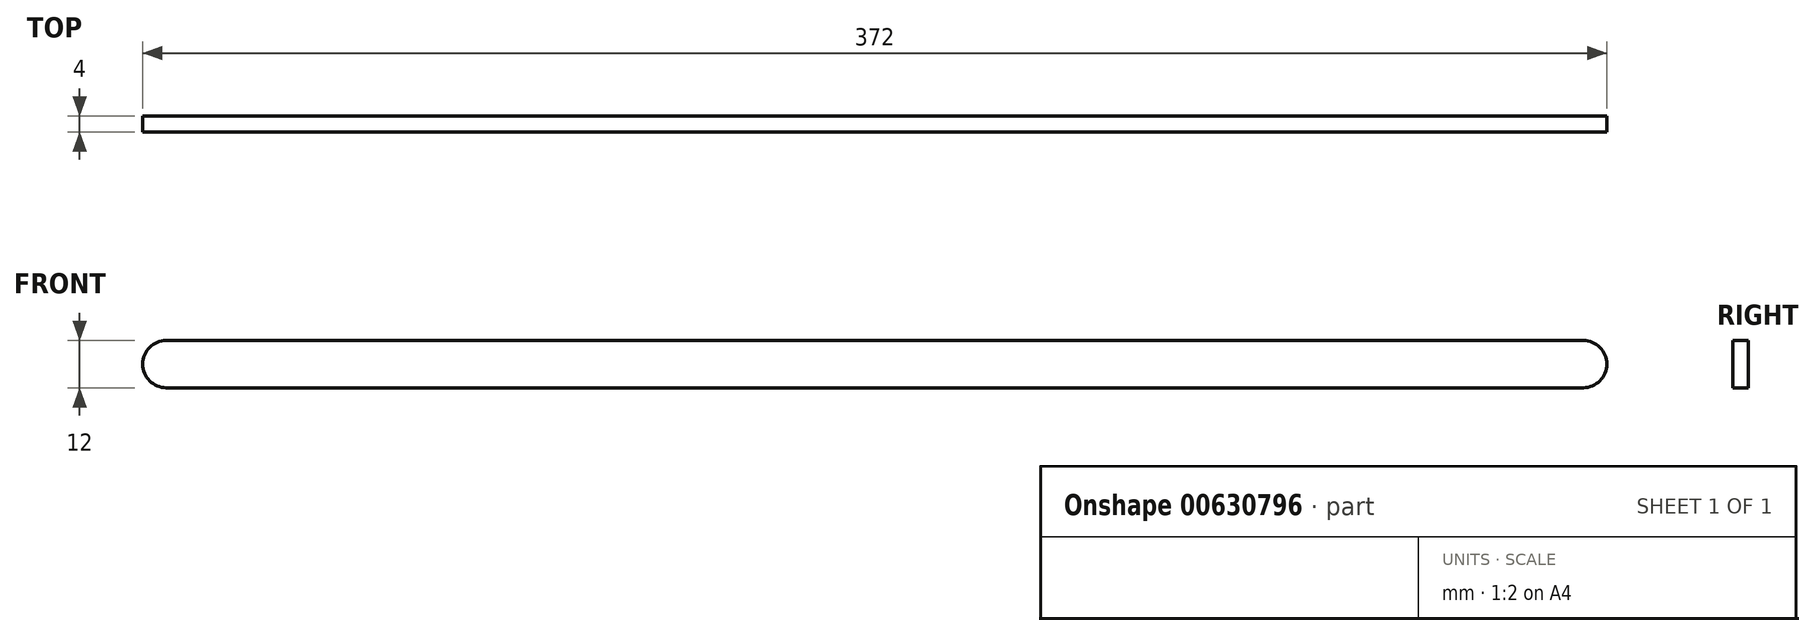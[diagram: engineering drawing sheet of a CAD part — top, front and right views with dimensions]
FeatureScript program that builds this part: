
annotation { "Feature Type Name" : "Feature", "Feature Type Description" : "" }
export const myFeature = defineFeature(function(context is Context, id is Id, definition is map)
    precondition{}
    {
        {
            var Q0;
            Q0=qCreatedBy(makeId("Front.planeOp"),FACE);
            var sketch = newSketch(context, id + "F0", { "sketchPlane" : qUnion([Q0])});
            skLineSegment(sketch, "E0", {"start": v(-28.06, 27.78) * mm, "end": v(331.94, 27.78) * mm});
            skArc(sketch, "E1.0.startCap", {"start": v(-28.06, 21.78) * mm, "mid": v(-34.06, 27.78) * mm, "end": v(-28.06, 33.78) * mm});
            skArc(sketch, "E1.0.endCap", {"start": v(331.94, 33.78) * mm, "mid": v(337.94, 27.78) * mm, "end": v(331.94, 21.78) * mm});
            skLineSegment(sketch, "E1.0.left", {"start": v(-28.06, 33.78) * mm, "end": v(331.94, 33.78) * mm});
            skLineSegment(sketch, "E1.0.right", {"start": v(-28.06, 21.78) * mm, "end": v(331.94, 21.78) * mm});
            skArc(sketch, "E2.0.startCap", {"start": v(-28.06, 20.98) * mm, "mid": v(-34.86, 27.78) * mm, "end": v(-28.06, 34.58) * mm});
            skArc(sketch, "E2.0.endCap", {"start": v(331.94, 34.58) * mm, "mid": v(338.74, 27.78) * mm, "end": v(331.94, 20.98) * mm});
            skLineSegment(sketch, "E2.0.left", {"start": v(-28.06, 34.58) * mm, "end": v(331.94, 34.58) * mm});
            skLineSegment(sketch, "E2.0.right", {"start": v(-28.06, 20.98) * mm, "end": v(331.94, 20.98) * mm});
            skSolve(sketch);
        }
        {
            var Q0;
            Q0=makeQuery(id+"F0.imprint","IMPRINT",FACE,{"disambiguationData":[TD([[makeQuery(id+"F0.imprint","IMPRINT",EDGE,{"derivedFrom":sQuery(id+"F0.wireOp",EDGE,"E1.0.startCap")}),1.0]])]});
            extrude(context, id + "F1", {"entities" : qUnion([Q0]), "depth" : 4 * mm, "offsetDistance" : 25 * mm});
        }
    });
